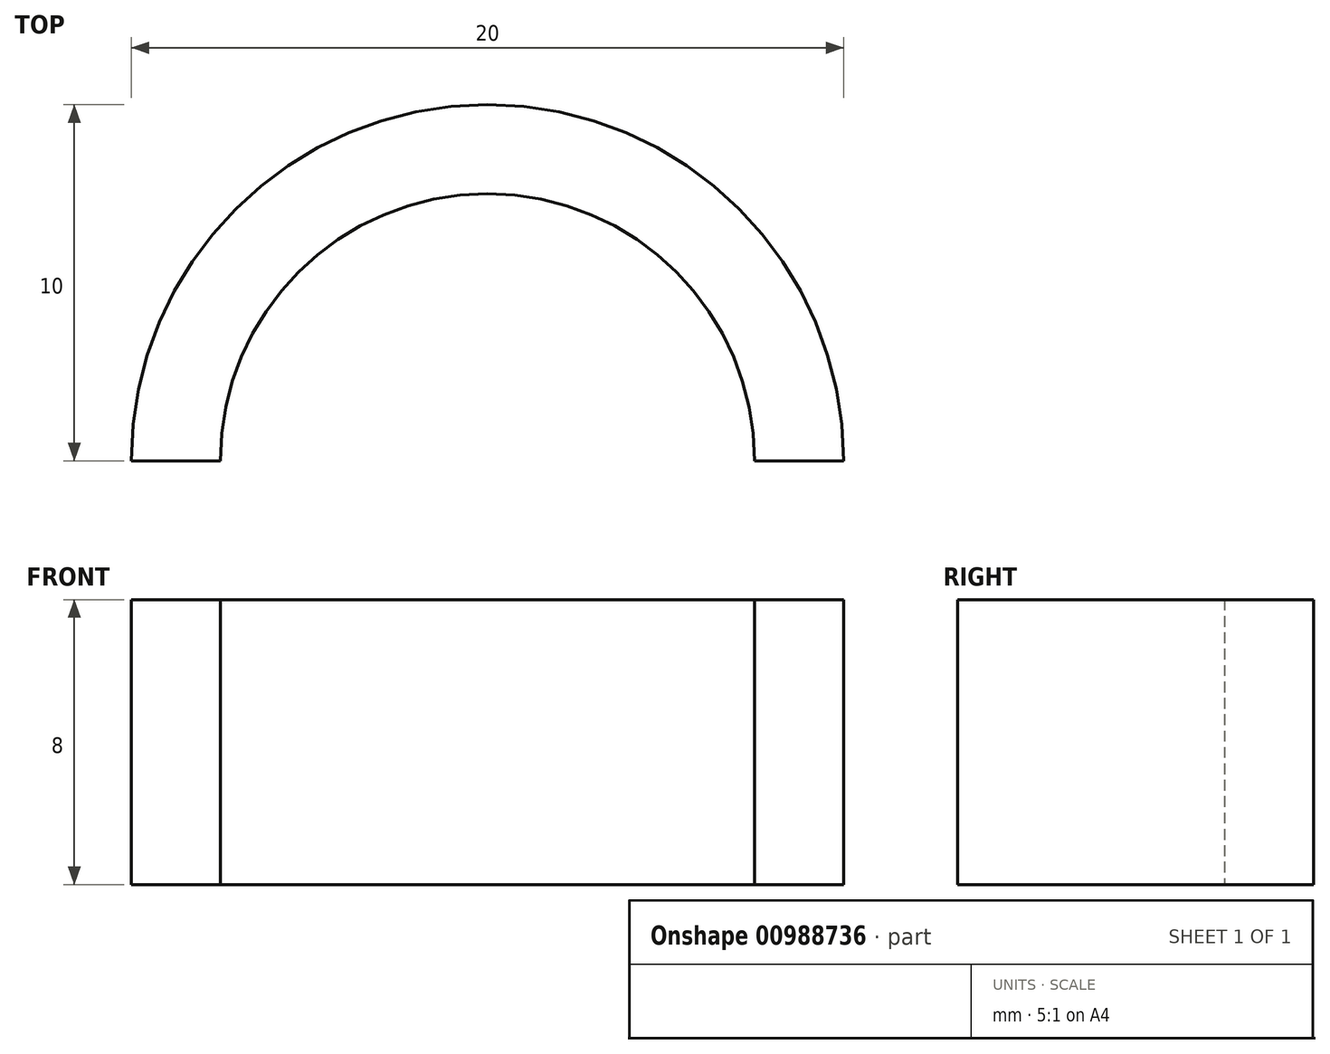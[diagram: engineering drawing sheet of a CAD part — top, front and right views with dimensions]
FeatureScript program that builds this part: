
annotation { "Feature Type Name" : "Feature", "Feature Type Description" : "" }
export const myFeature = defineFeature(function(context is Context, id is Id, definition is map)
    precondition{}
    {
        {
            var Q0;
            Q0=qCreatedBy(makeId("Top.planeOp"),FACE);
            var sketch = newSketch(context, id + "F0", { "sketchPlane" : qUnion([Q0])});
            skLineSegment(sketch, "E0", {"start": v(-10, 0) * mm, "end": v(10, 0) * mm});
            skArc(sketch, "E1", {"start": v(-7.5, 0) * mm, "mid": v(0, 7.5) * mm, "end": v(7.5, 0) * mm});
            skArc(sketch, "E2", {"start": v(-10, 0) * mm, "mid": v(0, 10) * mm, "end": v(10, 0) * mm});
            skArc(sketch, "E3", {"start": v(-2.5, 0) * mm, "mid": v(0, 2.5) * mm, "end": v(2.5, 0) * mm});
            skSolve(sketch);
        }
        {
            assignVariable(context, id + "F1", {"name" : "l", "anyValue" : 8});
        }
        {
            var Q0;
            {var subQ0=sQuery(id+"F0.wireOp",EDGE,"E1");Q0=makeQuery(id+"F0.imprint","IMPRINT",FACE,{"disambiguationData":[TD([[makeQuery(id+"F0.imprint","IMPRINT",EDGE,{"derivedFrom":subQ0}),-1.0]])]});}
            extrude(context, id + "F2", {"entities" : qUnion([Q0]), "depth" : (getVariable(context, 'l')) * mm, "offsetDistance" : 25 * mm});
        }
        {
            var Q0;
            Q0=qSketchRegion(id+"F0",true);
            extrude(context, id + "F3", {"entities" : qUnion([Q0]), "operationType" : NewBodyOperationType.ADD, "depth" : getVariable(context, 'l') / 2 * mm, "offsetDistance" : 25 * mm});
        }
        {
            var Q0;
            {var subQ1=sQuery(id+"F0.wireOp",EDGE,"E0");var subQ2=sQuery(id+"F0.wireOp",EDGE,"E3");Q0=makeQuery(id+"F3.boolean.opBoolean","SPLIT",FACE,{"disambiguationData":[TD([makeQuery(id+"F2.opExtrude","SWEPT_FACE",FACE,{"disambiguationData":[OSD([subQ2])]})])],"derivedFrom":makeQuery(id+"F3.opExtrude","CAP_FACE",FACE,{"disambiguationData":[OSD([subQ1,sQuery(id+"F0.wireOp",EDGE,"E2")])],"isStart":false})});}
            extrude(context, id + "F4", {"entities" : qUnion([Q0]), "operationType" : NewBodyOperationType.REMOVE, "oppositeDirection" : true, "depth" : 25 * mm, "offsetDistance" : 25 * mm});
        }
    });
